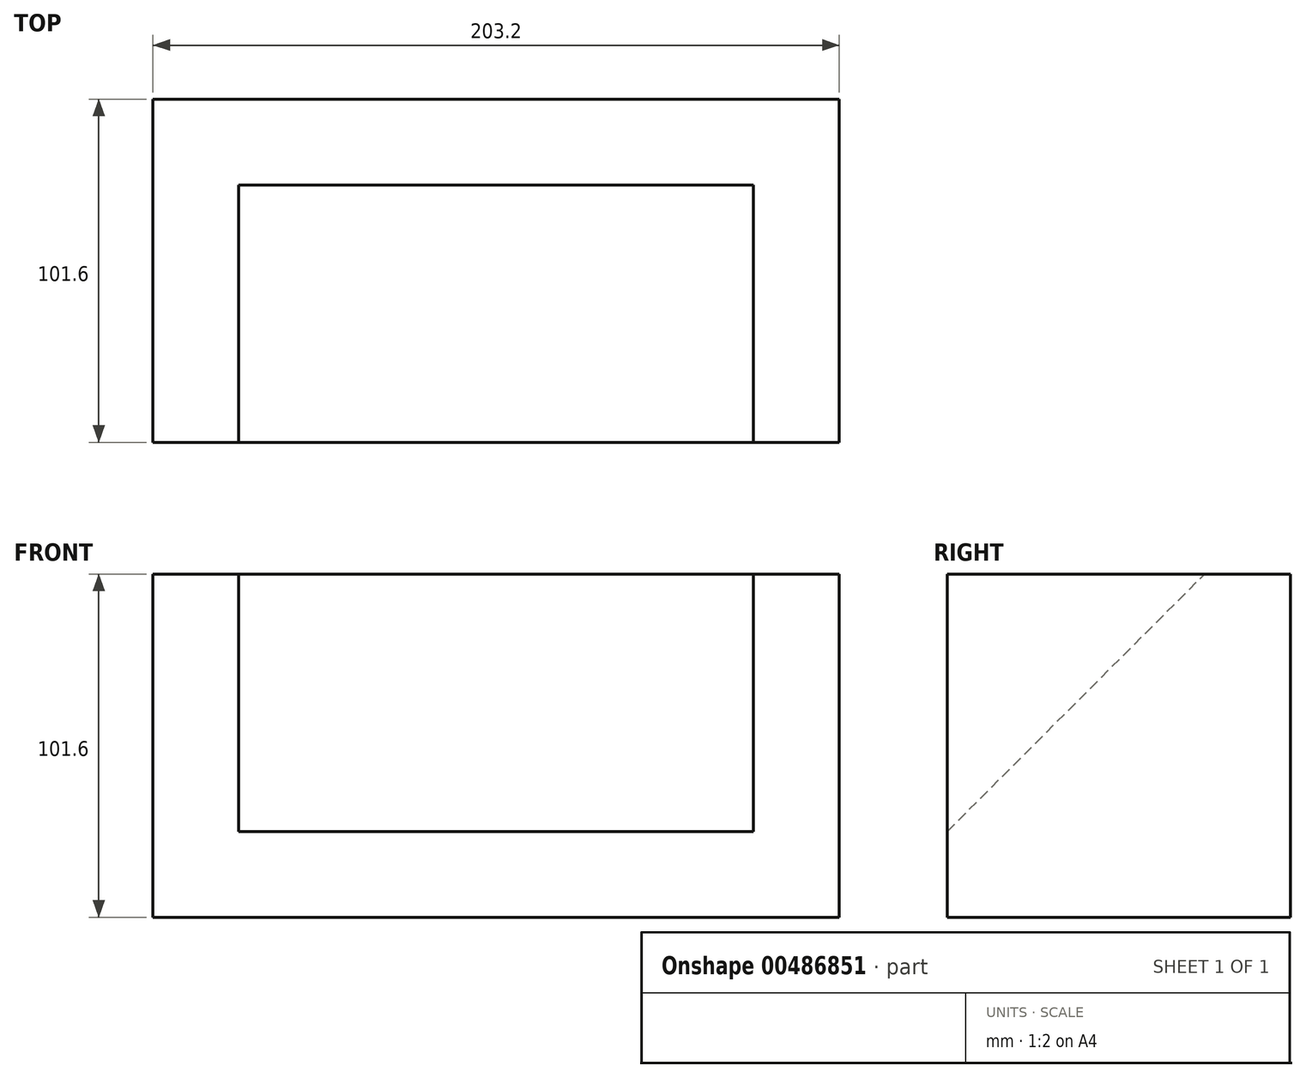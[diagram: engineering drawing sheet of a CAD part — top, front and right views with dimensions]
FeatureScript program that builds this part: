
annotation { "Feature Type Name" : "Feature", "Feature Type Description" : "" }
export const myFeature = defineFeature(function(context is Context, id is Id, definition is map)
    precondition{}
    {
        {
            var Q0;
            Q0=qCreatedBy(makeId("Right.planeOp"),FACE);
            var sketch = newSketch(context, id + "F0", { "sketchPlane" : qUnion([Q0])});
            skLineSegment(sketch, "E0.bottom", {"start": v(0, 0) * mm, "end": v(-101.6, 0) * mm});
            skLineSegment(sketch, "E0.top", {"start": v(0, 101.6) * mm, "end": v(-25.4, 101.6) * mm});
            skLineSegment(sketch, "E0.left", {"start": v(0, 0) * mm, "end": v(0, 101.6) * mm});
            skLineSegment(sketch, "E0.right", {"start": v(-101.6, 0) * mm, "end": v(-101.6, 25.4) * mm});
            skLineSegment(sketch, "E1", {"start": v(-101.6, 25.4) * mm, "end": v(-25.4, 101.6) * mm});
            skSolve(sketch);
        }
        {
            var Q0;
            Q0 = qSketchRegion(id + "F0", true);
            extrude(context, id + "F1", {"entities" : qUnion([Q0]), "depth" : 152.4 * mm});
        }
        {
            var Q0;
            Q0=makeQuery(id+"F1.opExtrude","CAP_FACE",FACE,{"disambiguationData":[OSD([sQuery(id+"F0.wireOp",EDGE,"E0.bottom"),sQuery(id+"F0.wireOp",EDGE,"E0.top"),sQuery(id+"F0.wireOp",EDGE,"E0.left"),sQuery(id+"F0.wireOp",EDGE,"E0.right"),sQuery(id+"F0.wireOp",EDGE,"E1")])],"isStart":true});
            var sketch = newSketch(context, id + "F2", { "sketchPlane" : qUnion([Q0])});
            skLineSegment(sketch, "E2.bottom", {"start": v(0, 0) * mm, "end": v(101.6, 0) * mm});
            skLineSegment(sketch, "E2.top", {"start": v(0, 101.6) * mm, "end": v(101.6, 101.6) * mm});
            skLineSegment(sketch, "E2.left", {"start": v(0, 0) * mm, "end": v(0, 101.6) * mm});
            skLineSegment(sketch, "E2.right", {"start": v(101.6, 0) * mm, "end": v(101.6, 101.6) * mm});
            skSolve(sketch);
        }
        {
            var Q0;
            Q0 = qSketchRegion(id + "F2", true);
            extrude(context, id + "F3", {"entities" : qUnion([Q0]), "operationType" : NewBodyOperationType.ADD, "depth" : 25.4 * mm});
        }
        {
            var Q0;
            Q0=makeQuery(id+"F1.opExtrude","CAP_FACE",FACE,{"disambiguationData":[OSD([sQuery(id+"F0.wireOp",EDGE,"E0.bottom"),sQuery(id+"F0.wireOp",EDGE,"E0.top"),sQuery(id+"F0.wireOp",EDGE,"E0.left"),sQuery(id+"F0.wireOp",EDGE,"E0.right"),sQuery(id+"F0.wireOp",EDGE,"E1")])],"isStart":false});
            var sketch = newSketch(context, id + "F4", { "sketchPlane" : qUnion([Q0])});
            skLineSegment(sketch, "E3.bottom", {"start": v(0, 0) * mm, "end": v(-101.6, 0) * mm});
            skLineSegment(sketch, "E3.top", {"start": v(0, 101.6) * mm, "end": v(-101.6, 101.6) * mm});
            skLineSegment(sketch, "E3.left", {"start": v(0, 0) * mm, "end": v(0, 101.6) * mm});
            skLineSegment(sketch, "E3.right", {"start": v(-101.6, 0) * mm, "end": v(-101.6, 101.6) * mm});
            skSolve(sketch);
        }
        {
            var Q0;
            Q0 = qSketchRegion(id + "F4", true);
            extrude(context, id + "F5", {"entities" : qUnion([Q0]), "operationType" : NewBodyOperationType.ADD, "depth" : 25.4 * mm});
        }
    });
